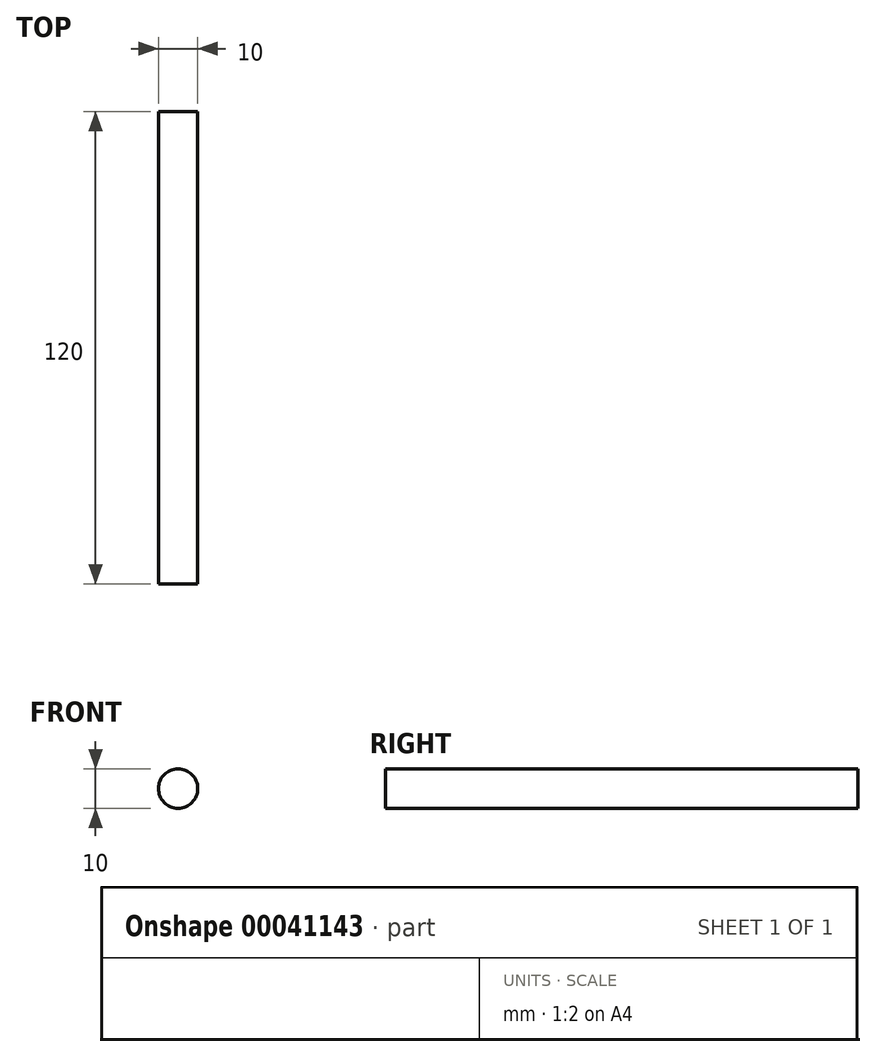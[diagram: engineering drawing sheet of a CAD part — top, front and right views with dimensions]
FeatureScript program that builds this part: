
annotation { "Feature Type Name" : "Feature", "Feature Type Description" : "" }
export const myFeature = defineFeature(function(context is Context, id is Id, definition is map)
    precondition{}
    {
        {
            var Q0;
            Q0=qCreatedBy(makeId("Front.planeOp"),FACE);
            var sketch = newSketch(context, id + "F0", { "sketchPlane" : qUnion([Q0])});
            skCircle(sketch, "E0", {"center": v(0, 0) * mm, "radius": 5 * mm});
            skSolve(sketch);
        }
        {
            var Q0;
            Q0=makeQuery(id+"F0.imprint","IMPRINT",FACE,{"disambiguationData":[TD([[makeQuery(id+"F0.imprint","IMPRINT",EDGE,{"derivedFrom":sQuery(id+"F0.wireOp",EDGE,"E0")}),1.0]])]});
            var Q1;
            Q1=sQuery(id+"F0.wireOp",EDGE,"E0");
            extrude(context, id + "F1", {"entities" : qUnion([Q0]), "surfaceEntities" : qUnion([Q1]), "depth" : 120 * mm});
        }
    });
